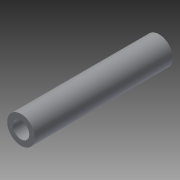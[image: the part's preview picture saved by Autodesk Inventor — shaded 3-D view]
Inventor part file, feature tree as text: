
AUTODESK INVENTOR PART (.ipt)
format: ipt  version: 2015 (Build 190159000, 159)  size: 74,240 bytes
history: native  units: mm
features: extrude x1, sketch x1
ambient origin geometry x8: Origin, YZ Plane, XZ Plane, XY Plane, X Axis, Y Axis, Z Axis, Center Point
bodies: Solid1 (feature_tree)
feature tree (2):
  extrude  "Extrusion1"  Depth=25.0mm
  sketch  "Sketch1"  dims[d0=3.0mm d1=5.0mm d2=25.0mm d3=0.0mm]
